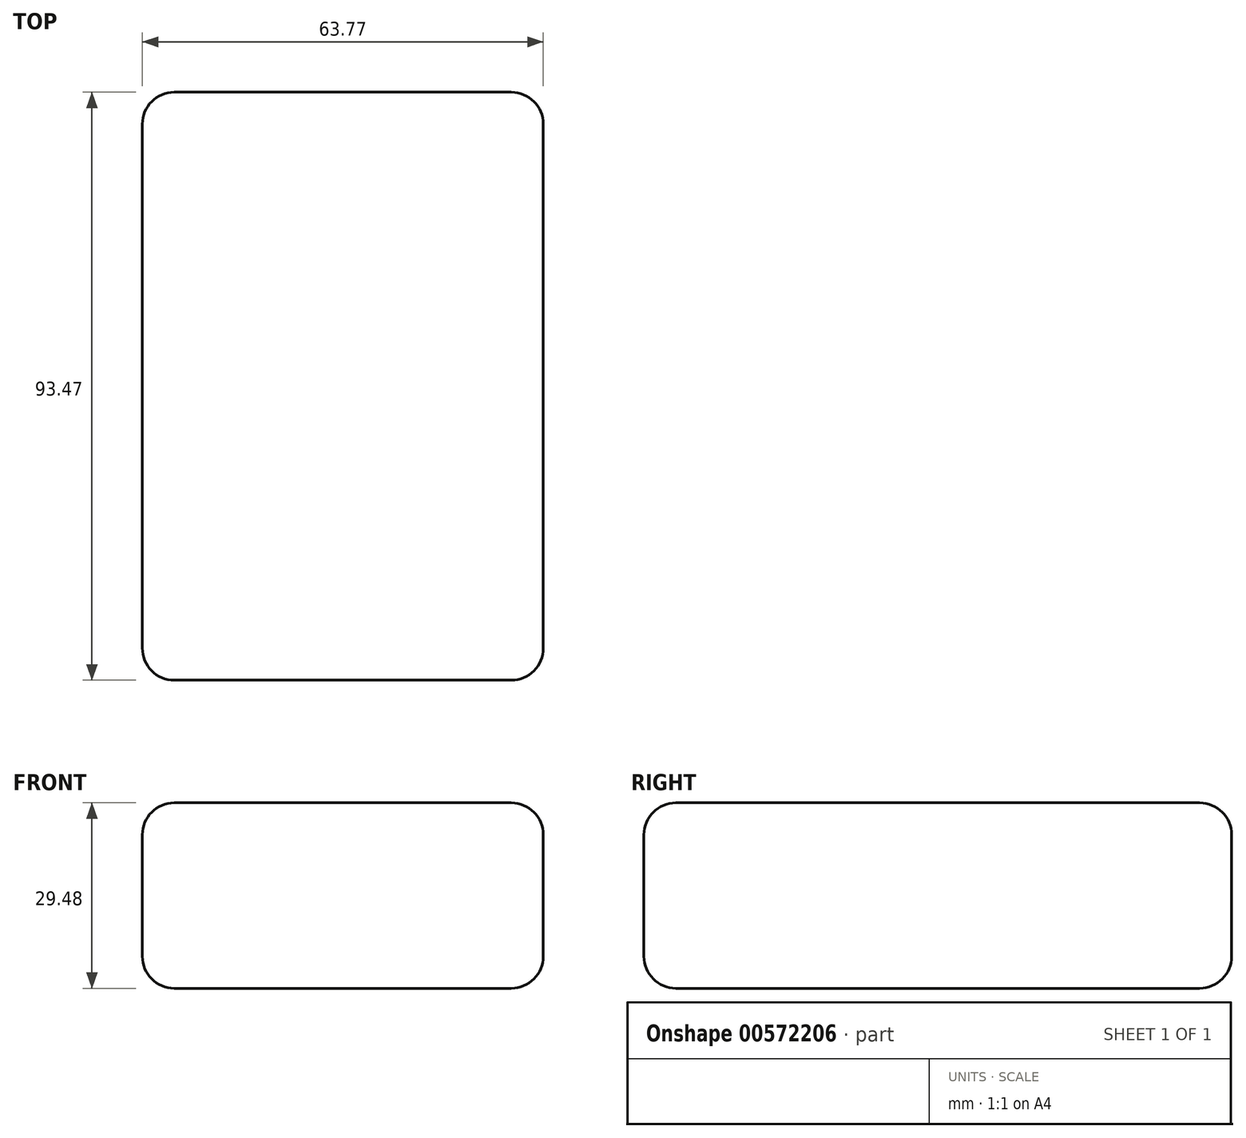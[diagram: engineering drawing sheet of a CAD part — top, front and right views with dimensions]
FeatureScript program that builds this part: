
annotation { "Feature Type Name" : "Feature", "Feature Type Description" : "" }
export const myFeature = defineFeature(function(context is Context, id is Id, definition is map)
    precondition{}
    {
        {
            var Q0;
            Q0=qCreatedBy(makeId("Front.planeOp"),FACE);
            var sketch = newSketch(context, id + "F0", { "sketchPlane" : qUnion([Q0])});
            skLineSegment(sketch, "E0.bottom", {"start": v(-34.9, 22.26) * mm, "end": v(28.88, 22.26) * mm});
            skLineSegment(sketch, "E0.top", {"start": v(-34.9, -7.22) * mm, "end": v(28.88, -7.22) * mm});
            skLineSegment(sketch, "E0.left", {"start": v(-34.9, 22.26) * mm, "end": v(-34.9, -7.22) * mm});
            skLineSegment(sketch, "E0.right", {"start": v(28.88, 22.26) * mm, "end": v(28.88, -7.22) * mm});
            skSolve(sketch);
        }
        {
            var Q0;
            Q0 = qSketchRegion(id + "F0", true);
            extrude(context, id + "F1", {"entities" : qUnion([Q0]), "depth" : 93.47 * mm, "offsetDistance" : 25.4 * mm});
        }
        {
            var Q0;
            Q0=makeQuery(id+"F1.opExtrude","CAP_FACE",FACE,{"disambiguationData":[OSD([sQuery(id+"F0.wireOp",EDGE,"E0.bottom"),sQuery(id+"F0.wireOp",EDGE,"E0.top"),sQuery(id+"F0.wireOp",EDGE,"E0.left"),sQuery(id+"F0.wireOp",EDGE,"E0.right")])],"isStart":false});
            var Q1;
            Q1=makeQuery(id+"F1.opExtrude","SWEPT_FACE",FACE,{"disambiguationData":[OSD([sQuery(id+"F0.wireOp",EDGE,"E0.right")])]});
            fillet(context, id + "F2", {"entities" : qUnion([Q0, Q1]), "radius" : 5.08 * mm, "tangentPropagation" : true, "allowEdgeOverflow" : false});
        }
        {
            var Q0;
            Q0=makeQuery(id+"F1.opExtrude","SWEPT_FACE",FACE,{"disambiguationData":[OSD([sQuery(id+"F0.wireOp",EDGE,"E0.left")])]});
            fillet(context, id + "F3", {"entities" : qUnion([Q0]), "radius" : 5.08 * mm, "tangentPropagation" : true, "allowEdgeOverflow" : false});
        }
        {
            var Q0;
            Q0=makeQuery(id+"F1.opExtrude","CAP_FACE",FACE,{"disambiguationData":[OSD([sQuery(id+"F0.wireOp",EDGE,"E0.bottom"),sQuery(id+"F0.wireOp",EDGE,"E0.top"),sQuery(id+"F0.wireOp",EDGE,"E0.left"),sQuery(id+"F0.wireOp",EDGE,"E0.right")])],"isStart":true});
            fillet(context, id + "F4", {"entities" : qUnion([Q0]), "radius" : 5.08 * mm, "tangentPropagation" : true, "allowEdgeOverflow" : false});
        }
        {
            var Q0;
            Q0=makeQuery(id+"F1.opExtrude","SWEPT_FACE",FACE,{"disambiguationData":[OSD([sQuery(id+"F0.wireOp",EDGE,"E0.bottom")])]});
            var sketch = newSketch(context, id + "F5", { "sketchPlane" : qUnion([Q0])});
            skCircle(sketch, "E1", {"center": v(-3.35, -68.91) * mm, "radius": 16.34 * mm});
            skCircle(sketch, "E2.0", {"center": v(-3.35, -68.91) * mm, "radius": 18.37 * mm});
            skSolve(sketch);
        }
        {
            var Q0;
            Q0=sQuery(id+"F5.wireOp",EDGE,"E1");
            var Q1;
            Q1=sQuery(id+"F5.wireOp",EDGE,"E2.0");
            extrude(context, id + "F6", {"bodyType" : ToolBodyType.SURFACE, "surfaceEntities" : qUnion([Q0, Q1]), "depth" : 6.86 * mm, "offsetDistance" : 25.4 * mm});
        }
    });
